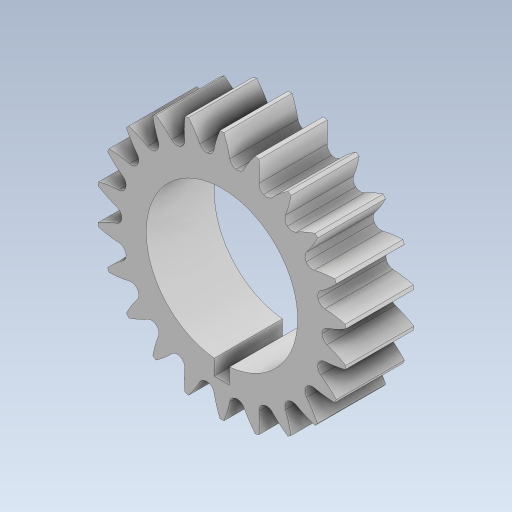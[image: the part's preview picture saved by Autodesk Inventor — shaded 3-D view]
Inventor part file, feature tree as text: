
AUTODESK INVENTOR PART (.ipt)
format: ipt  version: 2023.5 (Build 275446000, 446)  size: 587,776 bytes
history: native  units: in
note: dims shown in document units (in); Inventor stores cm internally (conversion verified against a paired STEP export)
features: extrude x2, sketch x1, fillet x1, pattern_circular x1
ambient origin geometry x8: Origin, YZ Plane, XZ Plane, XY Plane, X Axis, Y Axis, Z Axis, Center Point
bodies: Body1 (feature_tree)
feature tree (5):
  sketch  "Sketch1"  dims[d0=0.7874in d3=1.1811in d4=1.2992in d5=1.0433in d17=0.0394in d20=0.0618in d23=0.0925in d24=0.0197in d25=0.3543in d26=0.0in d27=0.3543in d28=0.0in d29=0.0394in d30=8.6614in d31=360.0deg d12=0.0197in d13=0.0344in d14=0.0197in d15=0.0344in]
  extrude  "Extrusion3"  Depth=0.0394in
  extrude  "Extrusion4"  Depth=0.0394in
  fillet  "Fillet2"  Radius=1.0433in
  pattern_circular  "Circular Pattern1"  [2 undecoded]
note: 2 required parameter values undecoded (feature->parameter linkage not recoverable at this tier; creation-order binding heuristic only, values carry confidence <= 0.55)
